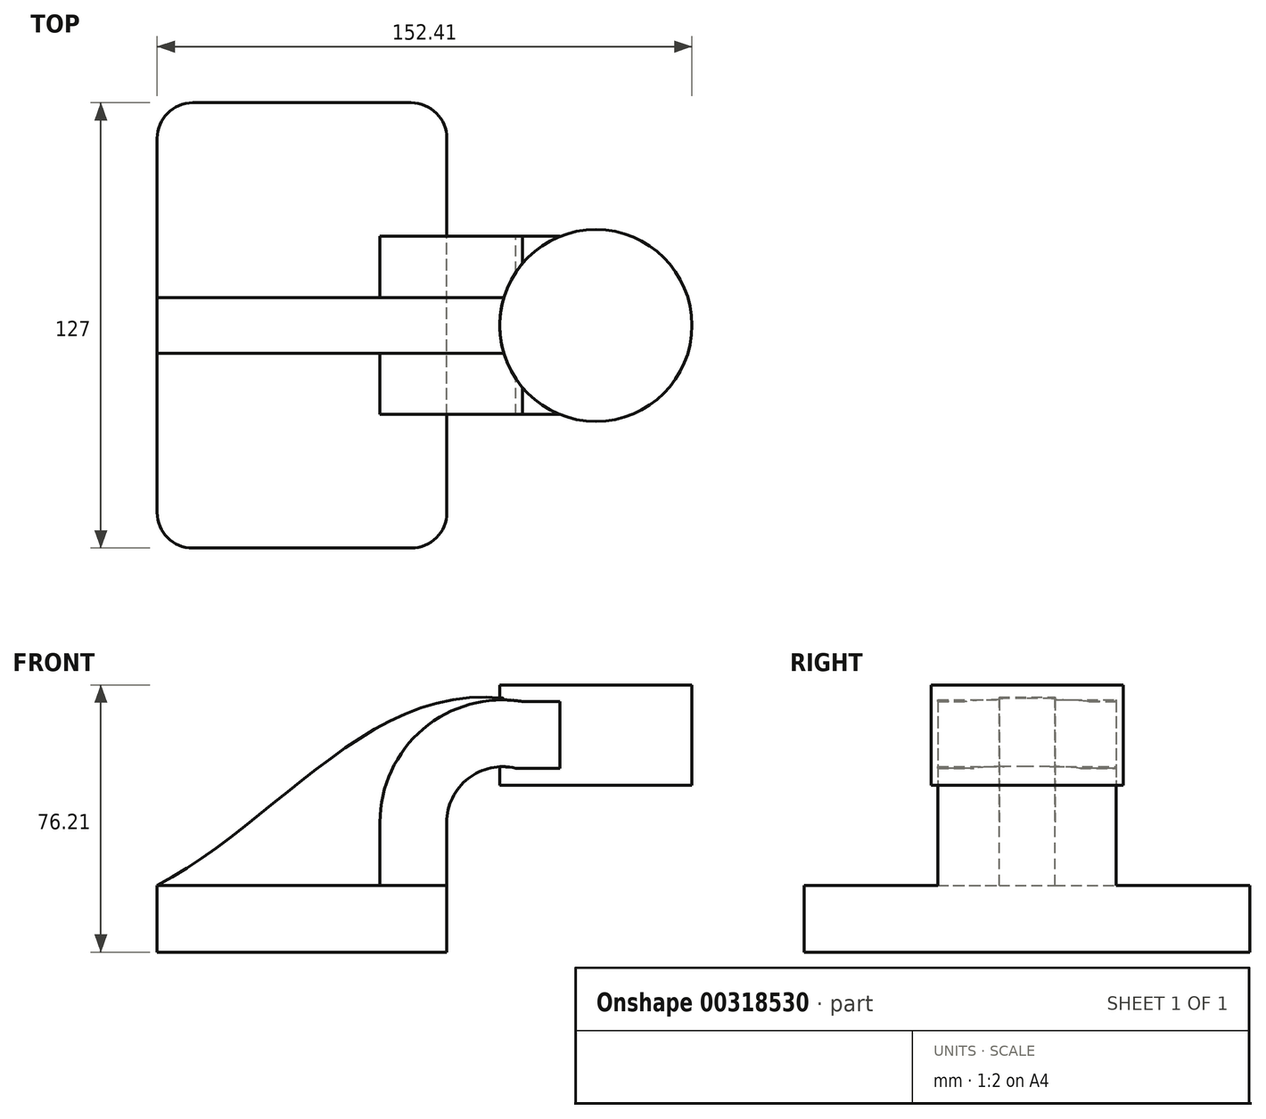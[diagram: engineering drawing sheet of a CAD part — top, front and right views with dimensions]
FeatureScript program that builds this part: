
annotation { "Feature Type Name" : "Feature", "Feature Type Description" : "" }
export const myFeature = defineFeature(function(context is Context, id is Id, definition is map)
    precondition{}
    {
        {
            var Q0;
            Q0=qCreatedBy(makeId("Front.planeOp"),FACE);
            var sketch = newSketch(context, id + "F0", { "sketchPlane" : qUnion([Q0])});
            skLineSegment(sketch, "E0.bottom", {"start": v(-41.28, 9.52) * mm, "end": v(41.28, 9.53) * mm});
            skLineSegment(sketch, "E0.top", {"start": v(-41.28, -9.53) * mm, "end": v(41.28, -9.53) * mm});
            skLineSegment(sketch, "E0.left", {"start": v(-41.28, 9.52) * mm, "end": v(-41.28, -9.53) * mm});
            skLineSegment(sketch, "E0.right", {"start": v(41.28, 9.53) * mm, "end": v(41.28, -9.52) * mm});
            skPoint(sketch, "E0.middle", {"position": v(0, 0) * mm});
            skLineSegment(sketch, "E1.bottom", {"start": v(111.12, 66.67) * mm, "end": v(60.32, 66.67) * mm});
            skLineSegment(sketch, "E1.top", {"start": v(111.12, 38.1) * mm, "end": v(60.32, 38.1) * mm});
            skLineSegment(sketch, "E1.left", {"start": v(111.12, 66.67) * mm, "end": v(111.12, 38.1) * mm});
            skLineSegment(sketch, "E1.right", {"start": v(60.32, 66.67) * mm, "end": v(60.32, 38.1) * mm});
            skPoint(sketch, "E1.middle", {"position": v(85.72, 52.39) * mm});
            skLineSegment(sketch, "E2", {"start": v(41.27, 9.53) * mm, "end": v(41.27, 27.47) * mm});
            skArc(sketch, "E3", {"start": v(41.27, 27.47) * mm, "mid": v(47.37, 39.97) * mm, "end": v(60.97, 42.88) * mm});
            skLineSegment(sketch, "E4", {"start": v(60.97, 42.88) * mm, "end": v(83.75, 42.88) * mm});
            skLineSegment(sketch, "E5.0", {"start": v(62.84, 61.93) * mm, "end": v(83.75, 61.93) * mm});
            skArc(sketch, "E5.1", {"start": v(22.22, 27.47) * mm, "mid": v(34.55, 54.1) * mm, "end": v(62.84, 61.93) * mm});
            skLineSegment(sketch, "E5.2", {"start": v(22.23, 9.53) * mm, "end": v(22.23, 27.47) * mm});
            skLineSegment(sketch, "E6", {"start": v(83.75, 38.1) * mm, "end": v(83.75, 66.67) * mm});
            skFitSpline(sketch, "E7", {"points": [v(-41.28, 9.52) * mm, v(62.84, 61.93) * mm], "startDerivative": vector(104.11, 52.4) * mm, "endDerivative": vector(124.35, -27.99) * mm});
            skSolve(sketch);
        }
        {
            var Q0;
            Q0=makeQuery(id+"F0.imprint","IMPRINT",FACE,{"disambiguationData":[TD([[makeQuery(id+"F0.imprint","IMPRINT",EDGE,{"derivedFrom":sQuery(id+"F0.wireOp",EDGE,"E0.top")}),1.0]])]});
            extrude(context, id + "F1", {"entities" : qUnion([Q0]), "endBound" : BoundingType.SYMMETRIC, "depth" : 127 * mm});
        }
        {
            var Q0;
            {var subQ1=sQuery(id+"F0.wireOp",EDGE,"E2");Q0=makeQuery(id+"F0.imprint","IMPRINT",FACE,{"disambiguationData":[TD([[makeQuery(id+"F0.imprint","IMPRINT",EDGE,{"derivedFrom":subQ1}),1.0]])]});}
            extrude(context, id + "F2", {"entities" : qUnion([Q0]), "operationType" : NewBodyOperationType.ADD, "endBound" : BoundingType.SYMMETRIC, "depth" : 50.8 * mm});
        }
        {
            var Q0;
            {var subQ1=sQuery(id+"F0.wireOp",EDGE,"E4");Q0=makeQuery(id+"F0.imprint","IMPRINT",FACE,{"disambiguationData":[TD([[makeQuery(id+"F0.imprint","IMPRINT",EDGE,{"derivedFrom":subQ1}),1.0]])]});}
            extrude(context, id + "F3", {"entities" : qUnion([Q0]), "operationType" : NewBodyOperationType.ADD, "endBound" : BoundingType.SYMMETRIC, "depth" : 50.8 * mm});
        }
        {
            var Q0;
            {var subQ0=sQuery(id+"F0.wireOp",EDGE,"E5.2");Q0=makeQuery(id+"F0.imprint","IMPRINT",FACE,{"disambiguationData":[TD([[makeQuery(id+"F0.imprint","IMPRINT",EDGE,{"derivedFrom":subQ0}),1.0]])]});}
            extrude(context, id + "F4", {"entities" : qUnion([Q0]), "operationType" : NewBodyOperationType.ADD, "endBound" : BoundingType.SYMMETRIC, "depth" : 15.88 * mm});
        }
        {
            var Q0;
            {var subQ0=sQuery(id+"F0.wireOp",EDGE,"E1.left");Q0=makeQuery(id+"F0.imprint","IMPRINT",FACE,{"disambiguationData":[TD([[makeQuery(id+"F0.imprint","IMPRINT",EDGE,{"derivedFrom":subQ0}),-1.0]])]});}
            var Q1;
            Q1=sQuery(id+"F0.wireOp",EDGE,"E6");
            revolve(context, id + "F5", {"operationType" : NewBodyOperationType.ADD, "entities" : qUnion([Q0]), "axis" : qUnion([Q1]), "revolveType" : RevolveType.FULL});
        }
        {
            var Q0;
            Q0=makeQuery(id+"F1.opExtrude","CAP_EDGE",EDGE,{"disambiguationData":[OSD([sQuery(id+"F0.wireOp",EDGE,"E0.right")])],"isStart":true});
            var Q1;
            Q1=makeQuery(id+"F1.opExtrude","CAP_EDGE",EDGE,{"disambiguationData":[OSD([sQuery(id+"F0.wireOp",EDGE,"E0.left")])],"isStart":true});
            var Q2;
            Q2=makeQuery(id+"F1.opExtrude","CAP_EDGE",EDGE,{"disambiguationData":[OSD([sQuery(id+"F0.wireOp",EDGE,"E0.right")])],"isStart":false});
            var Q3;
            Q3=makeQuery(id+"F1.opExtrude","CAP_EDGE",EDGE,{"disambiguationData":[OSD([sQuery(id+"F0.wireOp",EDGE,"E0.left")])],"isStart":false});
            fillet(context, id + "F6", {"entities" : qUnion([Q0, Q1, Q2, Q3]), "radius" : 10.16 * mm, "tangentPropagation" : true, "allowEdgeOverflow" : false});
        }
    });
